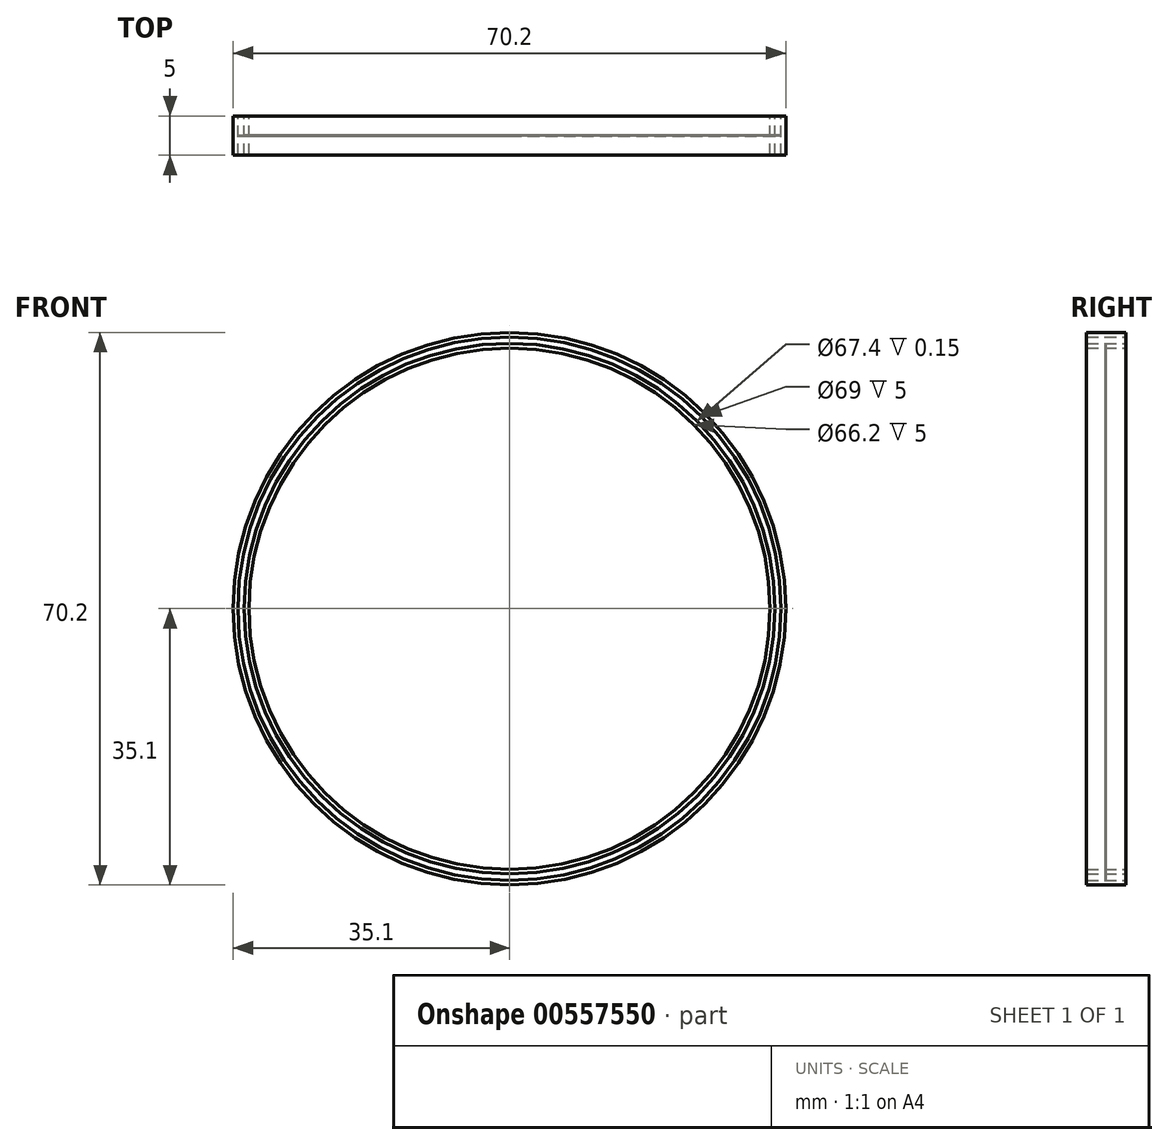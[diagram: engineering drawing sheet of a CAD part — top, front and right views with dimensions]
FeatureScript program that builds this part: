
annotation { "Feature Type Name" : "Feature", "Feature Type Description" : "" }
export const myFeature = defineFeature(function(context is Context, id is Id, definition is map)
    precondition{}
    {
        {
            var Q0;
            Q0=qCreatedBy(makeId("Front.planeOp"),FACE);
            var sketch = newSketch(context, id + "F0", { "sketchPlane" : qUnion([Q0])});
            skCircle(sketch, "E0", {"center": v(0, 0) * mm, "radius": 34.5 * mm});
            skCircle(sketch, "E1.0", {"center": v(0, 0) * mm, "radius": 35.1 * mm});
            skCircle(sketch, "E2.0", {"center": v(0, 0) * mm, "radius": 33.7 * mm});
            skCircle(sketch, "E3.0", {"center": v(0, 0) * mm, "radius": 33.1 * mm});
            skSolve(sketch);
        }
        {
            var Q0;
            Q0=makeQuery(id+"F0.imprint","IMPRINT",FACE,{"disambiguationData":[TD([[makeQuery(id+"F0.imprint","IMPRINT",EDGE,{"derivedFrom":sQuery(id+"F0.wireOp",EDGE,"E0")}),-1.0]])]});
            var Q1;
            Q1=makeQuery(id+"F0.imprint","IMPRINT",FACE,{"disambiguationData":[TD([[makeQuery(id+"F0.imprint","IMPRINT",EDGE,{"derivedFrom":sQuery(id+"F0.wireOp",EDGE,"E2.0")}),1.0]])]});
            extrude(context, id + "F1", {"entities" : qUnion([Q0, Q1]), "depth" : 5 * mm, "offsetDistance" : 25 * mm});
        }
        {
            var Q0;
            Q0=makeQuery(id+"F0.imprint","IMPRINT",FACE,{"disambiguationData":[TD([[makeQuery(id+"F0.imprint","IMPRINT",EDGE,{"derivedFrom":sQuery(id+"F0.wireOp",EDGE,"E3.0")}),1.0]])]});
            cPlane(context, id + "F2", {"entities" : qUnion([Q0]), "cplaneType" : CPlaneType.OFFSET, "offset" : 2.5 * mm, "width" : 150 * mm, "height" : 150 * mm});
        }
        {
            var Q0;
            Q0=qCreatedBy(id+"F2.planeOp",FACE);
            var sketch = newSketch(context, id + "F3", { "sketchPlane" : qUnion([Q0])});
            skCircle(sketch, "E4.0", {"center": v(0, 0) * mm, "radius": 34.5 * mm});
            skCircle(sketch, "E4.1", {"center": v(0, 0) * mm, "radius": 33.7 * mm});
            skSolve(sketch);
        }
        {
            var Q0;
            Q0=makeQuery(id+"F3.imprint","IMPRINT",FACE,{"disambiguationData":[TD([[makeQuery(id+"F3.imprint","IMPRINT",EDGE,{"derivedFrom":sQuery(id+"F3.wireOp",EDGE,"E4.0")}),1.0]])]});
            extrude(context, id + "F4", {"entities" : qUnion([Q0]), "endBound" : BoundingType.SYMMETRIC, "depth" : 0.15 * mm, "offsetDistance" : 25 * mm});
        }
    });
